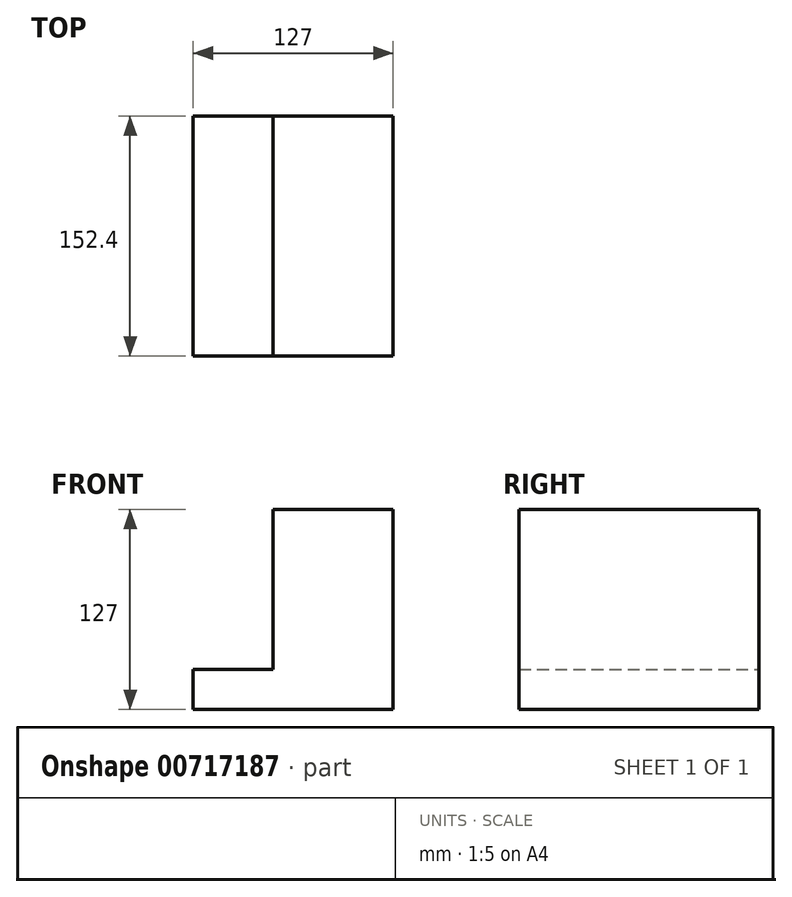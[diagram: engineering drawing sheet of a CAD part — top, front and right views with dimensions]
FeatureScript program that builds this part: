
annotation { "Feature Type Name" : "Feature", "Feature Type Description" : "" }
export const myFeature = defineFeature(function(context is Context, id is Id, definition is map)
    precondition{}
    {
        {
            var Q0;
            Q0=qCreatedBy(makeId("Front.planeOp"),FACE);
            var sketch = newSketch(context, id + "F0", { "sketchPlane" : qUnion([Q0])});
            skLineSegment(sketch, "E0", {"start": v(-57.82, -30.7) * mm, "end": v(69.18, -30.7) * mm});
            skLineSegment(sketch, "E1", {"start": v(69.18, -30.7) * mm, "end": v(69.18, 96.3) * mm});
            skLineSegment(sketch, "E2", {"start": v(69.18, 96.3) * mm, "end": v(-7.02, 96.3) * mm});
            skLineSegment(sketch, "E3", {"start": v(-7.02, 96.3) * mm, "end": v(-7.02, -5.3) * mm});
            skLineSegment(sketch, "E4", {"start": v(-7.02, -5.3) * mm, "end": v(-57.82, -5.3) * mm});
            skLineSegment(sketch, "E5", {"start": v(-57.82, -5.3) * mm, "end": v(-57.82, -30.7) * mm});
            skSolve(sketch);
        }
        {
            var Q0;
            Q0=makeQuery(id+"F0.imprint","IMPRINT",FACE,{"disambiguationData":[TD([[makeQuery(id+"F0.imprint","IMPRINT",EDGE,{"derivedFrom":sQuery(id+"F0.wireOp",EDGE,"E0")}),1.0]])]});
            extrude(context, id + "F1", {"entities" : qUnion([Q0]), "depth" : 152.4 * mm, "offsetDistance" : 25.4 * mm});
        }
    });
